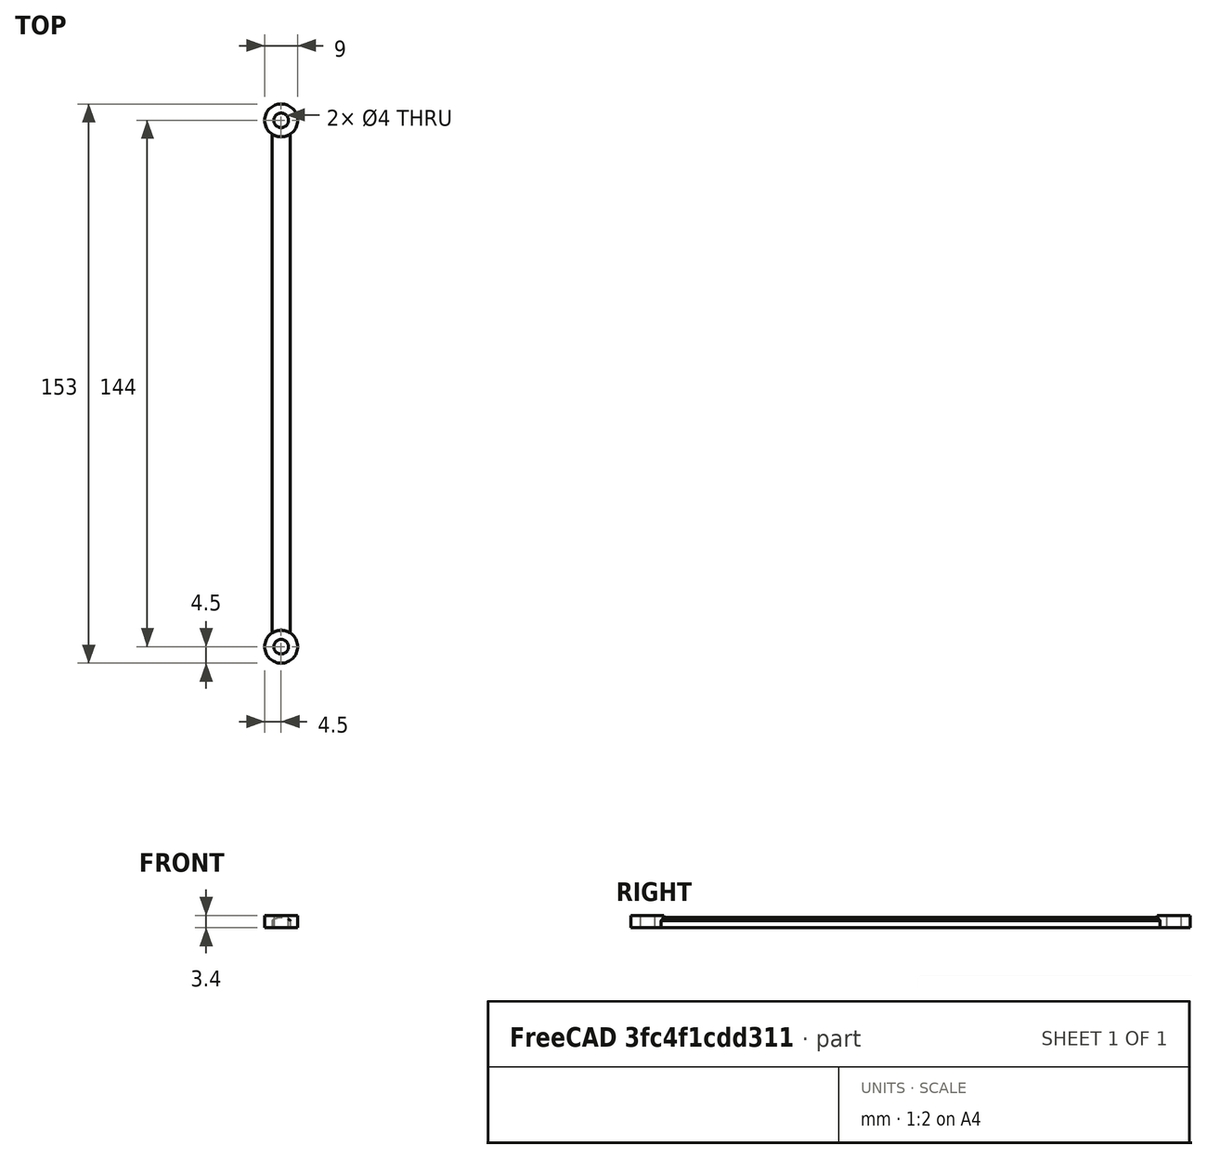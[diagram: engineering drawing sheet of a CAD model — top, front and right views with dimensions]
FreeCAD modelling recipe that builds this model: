
FCSTD DOCUMENT  (FreeCAD 0.19R24276 (Git))
Label: lanyard
License: All rights reserved
LicenseURL: http://en.wikipedia.org/wiki/All_rights_reserved
objects: Sketcher::SketchObject×2, PartDesign::Pad×2, PartDesign::Mirrored×1, PartDesign::Body×1, App::Part×1, Spreadsheet::Sheet×1, Mesh::Feature×1
note: 8 computed .brp shape members not serialized (recipe doc carries the construction recipe); baked Part::Feature solids carry a one-line shape summary decoded from their .brp

FEATURE [Sketcher::SketchObject] Sketch
  FullyConstrained = true
  MapMode = 5
  Placement = pos=(0,0,0) rot=(1,0,0;1.5708rad)
  Support = -> [XZ_Plane001]
  sketch-geometry (4):
    g0: LineSegment StartX=-2.5 StartY=0 StartZ=0 EndX=2.5 EndY=0 EndZ=0
    g1: LineSegment StartX=2.5 StartY=0 StartZ=0 EndX=2.5 EndY=2 EndZ=0
    g2: LineSegment StartX=-2.5 StartY=0 StartZ=0 EndX=-2.5 EndY=2 EndZ=0
    g3: ArcOfCircle CenterX=0 CenterY=-1.1225 CenterZ=0 NormalX=0 NormalY=0 NormalZ=1 AngleXU=0 Radius=4 StartAngle=0.895665 EndAngle=2.24593
  constraints (13):
    c: PointOnObject(g0,g-1)
    c: PointOnObject(g0,g-1)
    c: Coincident(g1,g0)
    c: Vertical(g1)
    c: Coincident(g2,g0)
    c: Vertical(g2)
    c: PointOnObject(g3,g-2)
    c: Coincident(g3,g2)
    c: Coincident(g3,g1)
    c: DistanceX(g0,g0) = 5
    c: Equal(g2,g1)
    c: DistanceY(g2,g2) = 2
    c: Radius(g3) = 4
FEATURE [PartDesign::Pad] Pad
  Direction = (1,1,1)
  Length = 140
  Length2 = 100
  Midplane = true
  Placement = pos=(0,0,0) rot=(1,0,0;1.5708rad)
  Profile = -> Sketch
  Type = 0
  expr: Length = Spreadsheet.length
FEATURE [Sketcher::SketchObject] Sketch001
  AttachmentOffset = pos=(0,72,0) rot=(0,0,1;0rad)
  FullyConstrained = true
  MapMode = 5
  Placement = pos=(0,72,0) rot=(0,0,1;0rad)
  Support = -> [XY_Plane001]
  expr: .AttachmentOffset.Base.y = Spreadsheet.length / 2 + 2
  expr: Constraints[2] = Spreadsheet.dia_inner / 2
  expr: Constraints[3] = Spreadsheet.dia_outer / 2
  sketch-geometry (2):
    g0: Circle CenterX=0 CenterY=0 CenterZ=0 NormalX=0 NormalY=0 NormalZ=1 AngleXU=0 Radius=2
    g1: Circle CenterX=0 CenterY=0 CenterZ=0 NormalX=0 NormalY=0 NormalZ=1 AngleXU=0 Radius=4.5
  constraints (4):
    c: Coincident(g0,g-1)
    c: Coincident(g1,g0)
    c: Radius(g0) = 2
    c: Radius(g1) = 4.5
FEATURE [PartDesign::Pad] Pad001
  BaseFeature = -> Pad
  Direction = (1,1,1)
  Length = 3.4
  Length2 = 100
  Placement = pos=(0,0,0) rot=(1,0,0;1.5708rad)
  Profile = -> Sketch001
  Type = 0
FEATURE [PartDesign::Mirrored] Mirrored
  BaseFeature = -> Pad001
  MirrorPlane = -> XZ_Plane001
  Originals = -> [Pad001]
  Placement = pos=(0,0,0) rot=(1,0,0;1.5708rad)
FEATURE [PartDesign::Body] Body
  Group = -> [Sketch,Pad,Sketch001,Pad001,Mirrored]
  Origin = -> Origin001
  Tip = -> Mirrored
FEATURE [App::Part] Part
  Group = -> [Body]
  Origin = -> Origin
FEATURE [Spreadsheet::Sheet] Spreadsheet
  cells = A1=length; B1(length)=140; A2=dia_inner; B2(dia_inner)=4; A3=dia_outer; B3(dia_outer)=9
FEATURE [Mesh::Feature] Mesh  label="Body (Meshed)"
